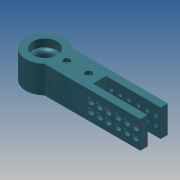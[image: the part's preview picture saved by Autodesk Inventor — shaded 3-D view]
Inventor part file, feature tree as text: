
AUTODESK INVENTOR PART (.ipt)
format: ipt  version: 2013 (Build 170138000, 138)  size: 295,424 bytes
history: native  units: mm
features: extrude x10, sketch x10, pattern_linear x2, fillet x1
ambient origin geometry x8: Origin, YZ Plane, XZ Plane, XY Plane, X Axis, Y Axis, Z Axis, Center Point
bodies: Solid1 (feature_tree)
feature tree (23):
  extrude  "Extrusion1"  Depth=12.6mm
  extrude  "Extrusion2"  Depth=8.5mm
  extrude  "Extrusion3"  Depth=22.0mm
  extrude  "Extrusion4"  Depth=20.0mm
  extrude  "Extrusion5"  Depth=7.0mm TaperAngle=0.0deg
  extrude  "Extrusion6"  Depth=3.5mm
  fillet  "Fillet1"  Radius=35.0mm
  extrude  "Extrusion7"  Depth=6.0mm
  extrude  "Extrusion8"  Depth=8.0mm TaperAngle=0.0deg
  extrude  "Extrusion9"  Depth=12.0mm
  extrude  "Extrusion10"  Depth=50.0mm
  pattern_linear  "Rectangular Pattern1"  Spacing1=10.0mm  [1 undecoded]
  pattern_linear  "Rectangular Pattern2"  Spacing1=12.5mm  [1 undecoded]
  sketch  "Sketch1"  dims[d0=150.0mm d2=12.6mm]
  sketch  "Sketch2"  dims[d3=15.0mm d4=8.5mm]
  sketch  "Sketch4"  dims[d5=25.0mm d6=0.0mm d7=22.0mm]
  sketch  "Sketch5"  dims[d9=7.0mm d10=0.0mm d16=20.0mm]
  sketch  "Sketch6"  dims[d17=40.0mm d18=7.0mm d19=0.0mm]
  sketch  "Sketch7"  dims[d21=3.0mm d22=0.0mm d23=3.5mm d24=35.0mm]
  sketch  "Sketch8"  dims[d26=10.0mm d27=0.0mm d28=6.0mm]
  sketch  "Sketch9"  dims[d30=14.0mm d32=8.0mm d33=0.0mm]
  sketch  "Sketch10"  dims[d34=3.5mm d35=12.0mm]
  sketch  "Sketch11"  dims[d37=50.0mm d38=50.0mm d39=10.0mm d40=0.0mm d41=12.5mm d42=8.0mm d43=3.5mm d44=10.0mm d45=0.0mm d46=6.0mm d48=3.0mm d49=0.0mm d50=5.5mm d51=4.0mm d52=0.0mm d53=30.0mm d55=8.0mm d56=20.0mm d58=8.0mm d59=20.0mm d61=25.0mm]
note: 2 required parameter values undecoded (feature->parameter linkage not recoverable at this tier; creation-order binding heuristic only, values carry confidence <= 0.55)
